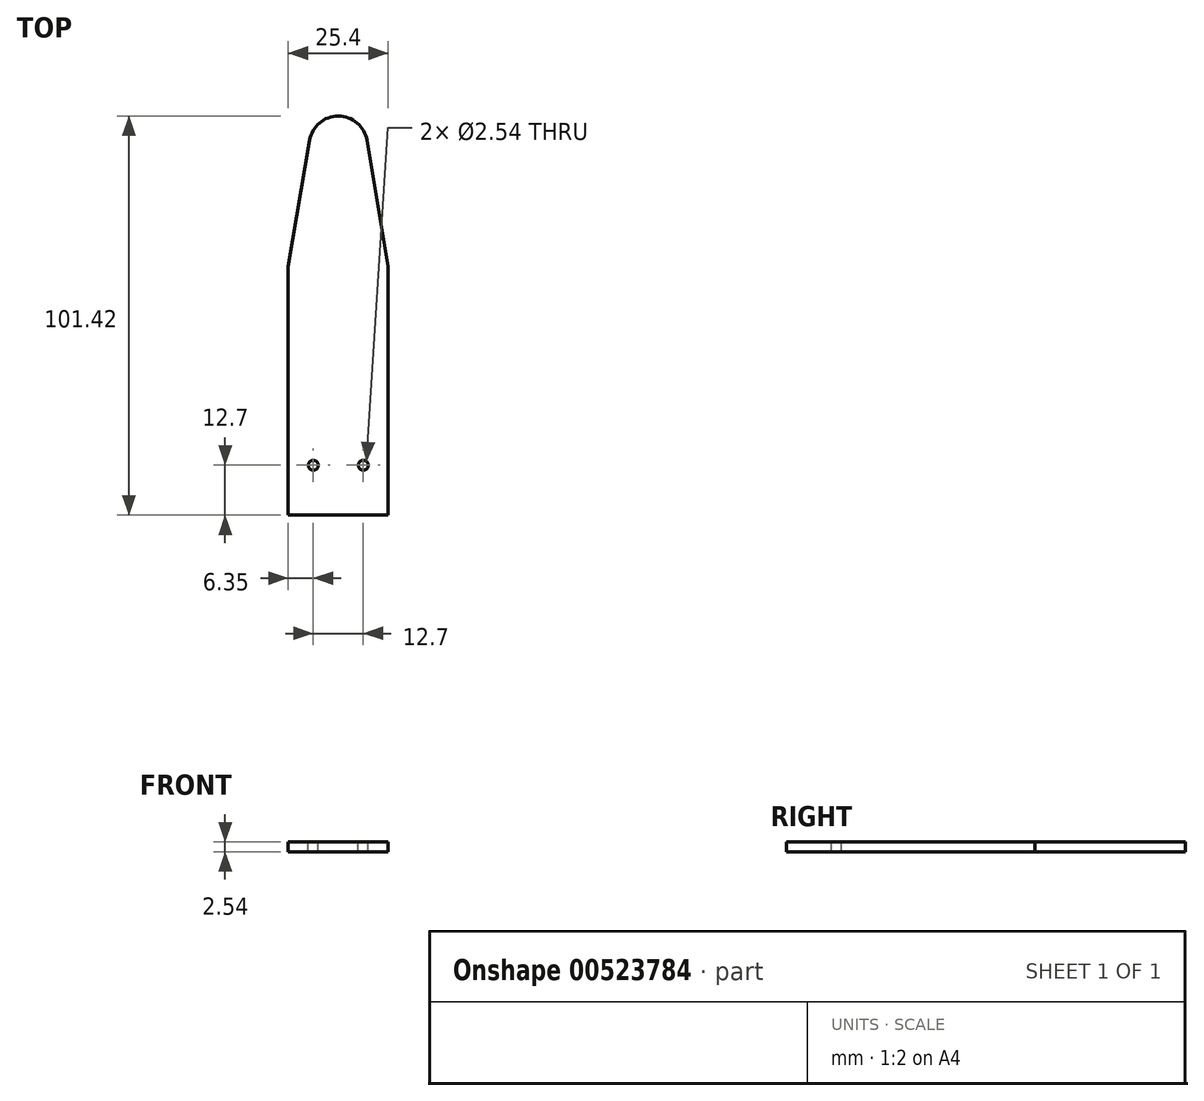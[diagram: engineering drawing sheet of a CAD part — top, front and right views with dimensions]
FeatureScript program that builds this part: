
annotation { "Feature Type Name" : "Feature", "Feature Type Description" : "" }
export const myFeature = defineFeature(function(context is Context, id is Id, definition is map)
    precondition{}
    {
        {
            var Q0;
            Q0=qCreatedBy(makeId("Top.planeOp"),FACE);
            var sketch = newSketch(context, id + "F0", { "sketchPlane" : qUnion([Q0])});
            skLineSegment(sketch, "E0", {"start": v(2.35, 0) * mm, "end": v(-23.05, 0) * mm});
            skLineSegment(sketch, "E1", {"start": v(-23.05, 0) * mm, "end": v(-23.05, 88.9) * mm});
            skLineSegment(sketch, "E2", {"start": v(-23.05, 88.9) * mm, "end": v(2.35, 88.9) * mm});
            skLineSegment(sketch, "E3", {"start": v(2.35, 88.9) * mm, "end": v(2.35, 0) * mm});
            skLineSegment(sketch, "E4", {"start": v(-23.05, 56.8) * mm, "end": v(-17.64, 88.9) * mm});
            skLineSegment(sketch, "E5", {"start": v(-10.35, 0) * mm, "end": v(-10.35, 8.23) * mm});
            skLineSegment(sketch, "E6.MirrorCS", {"start": v(2.35, 56.8) * mm, "end": v(-3.06, 88.9) * mm});
            skArc(sketch, "E7", {"start": v(-3.06, 88.9) * mm, "mid": v(-10.35, 95.07) * mm, "end": v(-17.64, 88.9) * mm});
            skSolve(sketch);
        }
        {
            var Q0;
            {var subQ0=sQuery(id+"F0.wireOp",EDGE,"E7");Q0=makeQuery(id+"F0.imprint","IMPRINT",FACE,{"disambiguationData":[TD([[makeQuery(id+"F0.imprint","IMPRINT",EDGE,{"derivedFrom":subQ0}),1.0]])]});}
            var Q1;
            {var subQ3=sQuery(id+"F0.wireOp",EDGE,"E4");Q1=makeQuery(id+"F0.imprint","IMPRINT",FACE,{"disambiguationData":[TD([[makeQuery(id+"F0.imprint","IMPRINT",EDGE,{"derivedFrom":subQ3}),-1.0]])]});}
            extrude(context, id + "F1", {"entities" : qUnion([Q0, Q1]), "depth" : 2.54 * mm, "offsetDistance" : 25.4 * mm});
        }
        {
            var Q0;
            Q0=makeQuery(id+"F1.opExtrude","CAP_FACE",FACE,{"disambiguationData":[OSD([sQuery(id+"F0.wireOp",EDGE,"E0"),sQuery(id+"F0.wireOp",EDGE,"E1"),sQuery(id+"F0.wireOp",EDGE,"E3"),sQuery(id+"F0.wireOp",EDGE,"E4"),sQuery(id+"F0.wireOp",EDGE,"E6.MirrorCS"),sQuery(id+"F0.wireOp",EDGE,"E7")])],"isStart":false});
            var sketch = newSketch(context, id + "F2", { "sketchPlane" : qUnion([Q0])});
            skLineSegment(sketch, "E8.bottom", {"start": v(-23.05, 0) * mm, "end": v(2.35, 0) * mm});
            skLineSegment(sketch, "E8.top", {"start": v(-23.05, 12.7) * mm, "end": v(2.35, 12.7) * mm});
            skLineSegment(sketch, "E8.left", {"start": v(-23.05, 0) * mm, "end": v(-23.05, 12.7) * mm});
            skLineSegment(sketch, "E8.right", {"start": v(2.35, 0) * mm, "end": v(2.35, 12.7) * mm});
            skLineSegment(sketch, "E9", {"start": v(-10.35, 0) * mm, "end": v(-10.35, 6.35) * mm});
            skLineSegment(sketch, "E10", {"start": v(-10.35, 6.35) * mm, "end": v(-4, 6.35) * mm});
            skLineSegment(sketch, "E11", {"start": v(-4, 6.35) * mm, "end": v(-16.7, 6.35) * mm});
            skCircle(sketch, "E12", {"center": v(-16.7, 6.35) * mm, "radius": 1.27 * mm});
            skCircle(sketch, "E13", {"center": v(-4, 6.35) * mm, "radius": 1.27 * mm});
            skSolve(sketch);
        }
        {
            var Q0;
            Q0=makeQuery(id+"F2.imprint","IMPRINT",FACE,{"disambiguationData":[TD([[makeQuery(id+"F2.imprint","IMPRINT",EDGE,{"derivedFrom":sQuery(id+"F2.wireOp",EDGE,"E12")}),1.0]])]});
            var Q1;
            Q1=makeQuery(id+"F2.imprint","IMPRINT",FACE,{"disambiguationData":[TD([[makeQuery(id+"F2.imprint","IMPRINT",EDGE,{"derivedFrom":sQuery(id+"F2.wireOp",EDGE,"E13")}),1.0]])]});
            extrude(context, id + "F3", {"entities" : qUnion([Q0, Q1]), "operationType" : NewBodyOperationType.REMOVE, "oppositeDirection" : true, "depth" : 25.4 * mm, "offsetDistance" : 25.4 * mm});
        }
        {
            var Q0;
            Q0=makeQuery(id+"F1.opExtrude","SWEPT_FACE",FACE,{"disambiguationData":[OSD([sQuery(id+"F0.wireOp",EDGE,"E0")])]});
            extrude(context, id + "F4", {"entities" : qUnion([Q0]), "operationType" : NewBodyOperationType.ADD, "depth" : 6.35 * mm, "offsetDistance" : 25.4 * mm});
        }
    });
